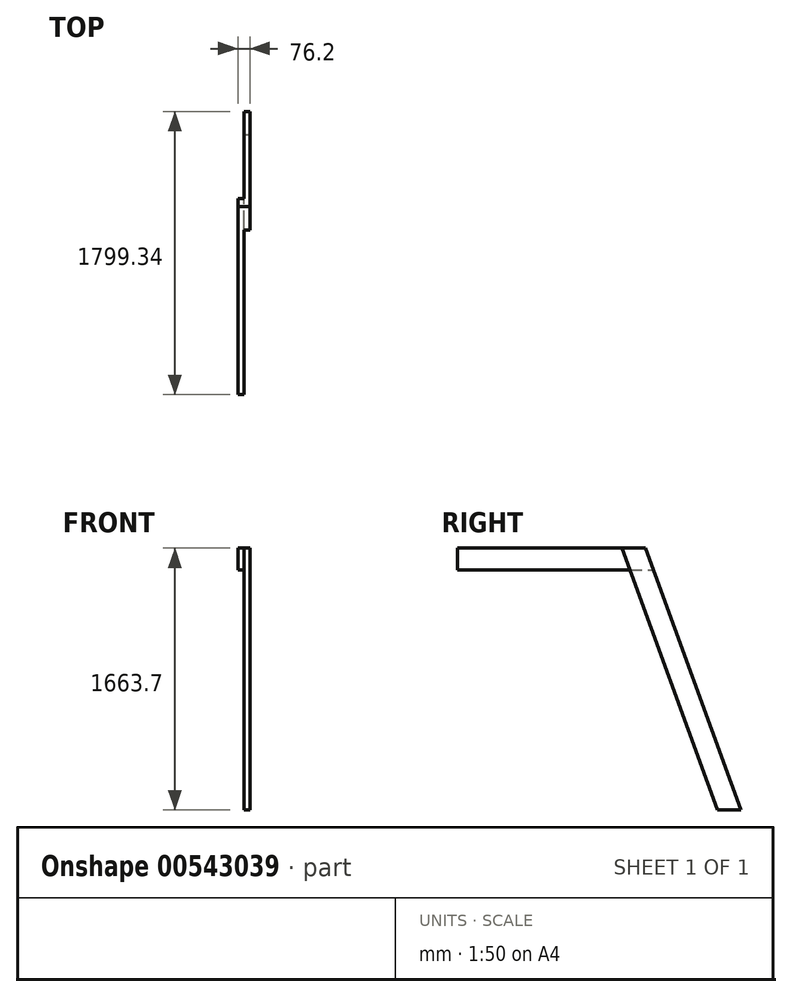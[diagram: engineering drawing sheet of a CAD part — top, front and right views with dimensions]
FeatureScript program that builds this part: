
annotation { "Feature Type Name" : "Feature", "Feature Type Description" : "" }
export const myFeature = defineFeature(function(context is Context, id is Id, definition is map)
    precondition{}
    {
        {
            var Q0;
            Q0=qCreatedBy(makeId("Right.planeOp"),FACE);
            var sketch = newSketch(context, id + "F0", { "sketchPlane" : qUnion([Q0])});
            skLineSegment(sketch, "E0", {"start": v(0, 0) * mm, "end": v(0, 2438.4) * mm});
            skLineSegment(sketch, "E1", {"start": v(0, 2438.4) * mm, "end": v(508, 2438.4) * mm});
            skLineSegment(sketch, "E2", {"start": v(508, 2438.4) * mm, "end": v(508, 2590.8) * mm});
            skLineSegment(sketch, "E3", {"start": v(508, 2590.8) * mm, "end": v(0, 2844.8) * mm});
            skLineSegment(sketch, "E4.bottom", {"start": v(584.2, 1676.4) * mm, "end": v(1193.8, 1676.4) * mm});
            skLineSegment(sketch, "E4.top", {"start": v(584.2, 1663.7) * mm, "end": v(1193.8, 1663.7) * mm});
            skLineSegment(sketch, "E4.left", {"start": v(584.2, 1676.4) * mm, "end": v(584.2, 1663.7) * mm});
            skLineSegment(sketch, "E4.right", {"start": v(1193.8, 1676.4) * mm, "end": v(1193.8, 1663.7) * mm});
            skLineSegment(sketch, "E5.bottom", {"start": v(584.2, 1663.7) * mm, "end": v(622.3, 1663.7) * mm});
            skLineSegment(sketch, "E5.top", {"start": v(584.2, 1524) * mm, "end": v(622.3, 1524) * mm});
            skLineSegment(sketch, "E5.left", {"start": v(584.2, 1663.7) * mm, "end": v(584.2, 1524) * mm});
            skLineSegment(sketch, "E5.right", {"start": v(622.3, 1663.7) * mm, "end": v(622.3, 1524) * mm});
            skLineSegment(sketch, "E6.bottom", {"start": v(1193.8, 1663.7) * mm, "end": v(1155.7, 1663.7) * mm});
            skLineSegment(sketch, "E6.top", {"start": v(1193.8, 1524) * mm, "end": v(1155.7, 1524) * mm});
            skLineSegment(sketch, "E6.left", {"start": v(1193.8, 1663.7) * mm, "end": v(1193.8, 1524) * mm});
            skLineSegment(sketch, "E6.right", {"start": v(1155.7, 1663.7) * mm, "end": v(1155.7, 1524) * mm});
            skLineSegment(sketch, "E7", {"start": v(1650.67, 0) * mm, "end": v(1799.34, 0) * mm});
            skLineSegment(sketch, "E8", {"start": v(1799.34, 0) * mm, "end": v(1193.8, 1663.7) * mm});
            skLineSegment(sketch, "E9", {"start": v(1193.8, 1663.7) * mm, "end": v(1045.13, 1663.7) * mm});
            skLineSegment(sketch, "E10", {"start": v(1045.13, 1663.7) * mm, "end": v(1650.67, 0) * mm});
            skLineSegment(sketch, "E11", {"start": v(1193.8, 1663.7) * mm, "end": v(0, 1663.7) * mm});
            skLineSegment(sketch, "E12", {"start": v(0, 1663.7) * mm, "end": v(0, 1524) * mm});
            skLineSegment(sketch, "E13", {"start": v(0, 1524) * mm, "end": v(1244.65, 1524) * mm});
            skLineSegment(sketch, "E14", {"start": v(1244.65, 1524) * mm, "end": v(1193.8, 1663.7) * mm});
            skSolve(sketch);
        }
        {
            var Q0;
            {var subQ4=sQuery(id+"F0.wireOp",EDGE,"E7");Q0=makeQuery(id+"F0.imprint","IMPRINT",FACE,{"disambiguationData":[TD([[makeQuery(id+"F0.imprint","IMPRINT",EDGE,{"derivedFrom":subQ4}),1.0]])]});}
            var Q1;
            {var subQ0=sQuery(id+"F0.wireOp",EDGE,"E6.right");Q1=makeQuery(id+"F0.imprint","IMPRINT",FACE,{"disambiguationData":[TD([[makeQuery(id+"F0.imprint","IMPRINT",EDGE,{"derivedFrom":subQ0}),-1.0]])]});}
            var Q2;
            {var subQ0=sQuery(id+"F0.wireOp",EDGE,"E6.left");Q2=makeQuery(id+"F0.imprint","IMPRINT",FACE,{"disambiguationData":[TD([[makeQuery(id+"F0.imprint","IMPRINT",EDGE,{"derivedFrom":subQ0}),-1.0]])]});}
            var Q3;
            {var subQ0=sQuery(id+"F0.wireOp",EDGE,"E6.left");Q3=makeQuery(id+"F0.imprint","IMPRINT",FACE,{"disambiguationData":[TD([[makeQuery(id+"F0.imprint","IMPRINT",EDGE,{"derivedFrom":subQ0}),1.0]])]});}
            extrude(context, id + "F1", {"entities" : qUnion([Q0, Q1, Q2, Q3]), "depth" : 38.1 * mm, "offsetDistance" : 25.4 * mm});
        }
        {
            var Q0;
            {var subQ0=sQuery(id+"F0.wireOp",EDGE,"E5.left");Q0=makeQuery(id+"F0.imprint","IMPRINT",FACE,{"disambiguationData":[TD([[makeQuery(id+"F0.imprint","IMPRINT",EDGE,{"derivedFrom":subQ0}),-1.0]])]});}
            var Q1;
            {var subQ0=sQuery(id+"F0.wireOp",EDGE,"E5.left");Q1=makeQuery(id+"F0.imprint","IMPRINT",FACE,{"disambiguationData":[TD([[makeQuery(id+"F0.imprint","IMPRINT",EDGE,{"derivedFrom":subQ0}),1.0]])]});}
            var Q2;
            {var subQ0=sQuery(id+"F0.wireOp",EDGE,"E5.right");Q2=makeQuery(id+"F0.imprint","IMPRINT",FACE,{"disambiguationData":[TD([[makeQuery(id+"F0.imprint","IMPRINT",EDGE,{"derivedFrom":subQ0}),1.0]])]});}
            var Q3;
            {var subQ0=sQuery(id+"F0.wireOp",EDGE,"E6.right");Q3=makeQuery(id+"F0.imprint","IMPRINT",FACE,{"disambiguationData":[TD([[makeQuery(id+"F0.imprint","IMPRINT",EDGE,{"derivedFrom":subQ0}),-1.0]])]});}
            var Q4;
            {var subQ0=sQuery(id+"F0.wireOp",EDGE,"E6.left");Q4=makeQuery(id+"F0.imprint","IMPRINT",FACE,{"disambiguationData":[TD([[makeQuery(id+"F0.imprint","IMPRINT",EDGE,{"derivedFrom":subQ0}),-1.0]])]});}
            var Q5;
            {var subQ0=sQuery(id+"F0.wireOp",EDGE,"E6.left");Q5=makeQuery(id+"F0.imprint","IMPRINT",FACE,{"disambiguationData":[TD([[makeQuery(id+"F0.imprint","IMPRINT",EDGE,{"derivedFrom":subQ0}),1.0]])]});}
            extrude(context, id + "F2", {"entities" : qUnion([Q0, Q1, Q2, Q3, Q4, Q5]), "operationType" : NewBodyOperationType.ADD, "depth" : 0 * mm, "offsetDistance" : 25.4 * mm, "hasSecondDirection" : true, "secondDirectionOppositeDirection" : true, "secondDirectionDepth" : 38.1 * mm});
        }
    });
